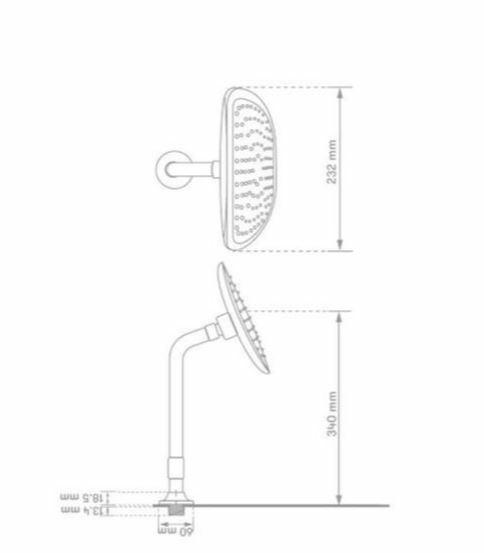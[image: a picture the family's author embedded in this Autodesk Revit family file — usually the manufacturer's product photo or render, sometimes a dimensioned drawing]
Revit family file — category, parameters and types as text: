
# Revit family: 01-3635-211 MEZCLADOR DUCHA 8” SIN SALIDA TINA FIRENZE PALA
name_source: partatom
category: Plumbing Fixtures
revit_build: Autodesk Revit 2018 (Build: 20170223_1515(x64)
units: mm (PartAtom-declared; Revit-internal decimal feet)

## family parameters
Cut with Voids When Loaded = No
Host = Face
OmniClass Number = 23.31.11.00
Part Type = Normal
Room Calculation Point = No
Round Connector Dimension = Use Diameter
Shared = No

## types (1)
- 01-3635-211
    Acero inoxidable = Metal Acero Inoxidable Cromado
    Ancho escudo = 53 mm  [stored 0.173885 ft]
    CW Connection = Yes
    Default Elevation = 0 mm  [stored 0 ft]
    Description = Mezclador ducha
    Distancia entre griferias = 203.2 mm  [stored 0.666667 ft]
    HW Connection = Yes
    Link Ficha Tecnica = No encontrada en internet
    Manija = 65 mm
    Manufacturer = Gricol
    Metal Laton Cromado = Metal Laton Cromado
    Model = 01-3635-211
    Plastico ABS Cromado = Plastico - ABS Cromado
    Product Name = DUCHA 8” SIN SALIDA TINA FIRENZE PALA
    Type Image = <None>
    URL = https://www.gricol.com
    Vent Connection = No
    Waste Connection = No

note: [stored X ft] marks values corroborated as IEEE doubles in the binary element streams (Revit-internal decimal feet)

## geometry (parser evidence)
native form markers: Blend x2, Sweep x9
no freeform markers — native parametric forms only
